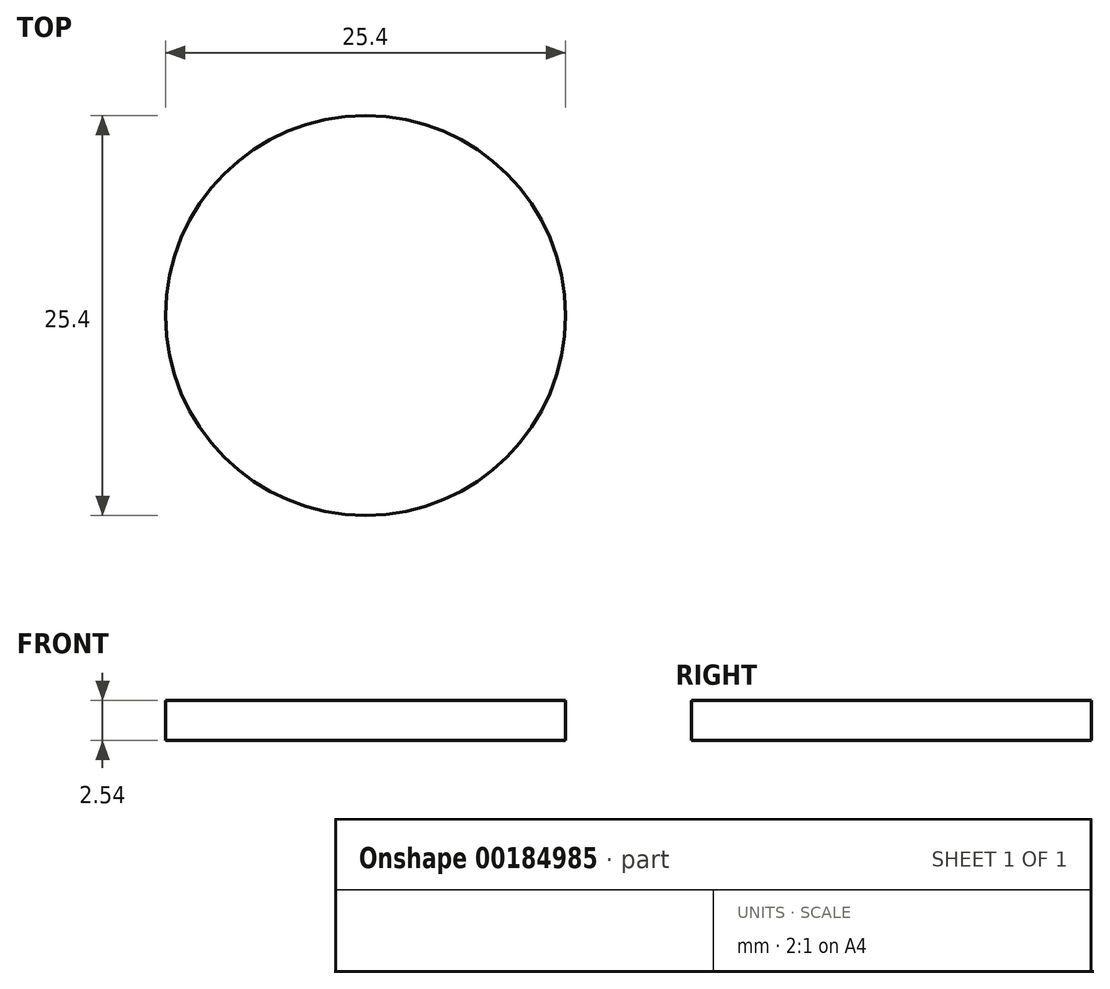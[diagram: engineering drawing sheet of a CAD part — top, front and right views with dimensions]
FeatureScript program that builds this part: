
annotation { "Feature Type Name" : "Feature", "Feature Type Description" : "" }
export const myFeature = defineFeature(function(context is Context, id is Id, definition is map)
    precondition{}
    {
        {
            var Q0;
            Q0=qCreatedBy(makeId("Top.planeOp"),FACE);
            var sketch = newSketch(context, id + "F0", { "sketchPlane" : qUnion([Q0])});
            skCircle(sketch, "E0", {"center": v(0, 0) * mm, "radius": 12.7 * mm});
            skSolve(sketch);
        }
        {
            var Q0;
            Q0 = qSketchRegion(id + "F0", true);
            extrude(context, id + "F1", {"entities" : qUnion([Q0]), "depth" : 2.54 * mm});
        }
    });
